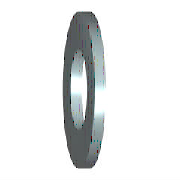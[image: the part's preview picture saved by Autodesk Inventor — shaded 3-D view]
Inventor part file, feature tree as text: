
AUTODESK INVENTOR PART (.ipt)
format: ipt  version: 2022 (Build 260153000, 153)  size: 107,008 bytes
history: native  units: mm (DEFAULTED — no unit token found)
features: extrude x1, other x1, plane x1, sketch x1
ambient origin geometry x7: Origin, YZ Plane, XY Plane, X Axis, Y Axis, Z Axis, Center Point
bodies: Solid1 (feature_tree)
feature tree (4):
  extrude  "Базовый элемент"  Depth=4.8mm
  other  "Work Axis1"
  plane  "Work Plane1"
  sketch  "Эскиз"
